# Revit family: ElectricalFixture_WiringAccessories_Hager_Sollysta_WhiteMetalcladEuroPlates
name_source: partatom
category: Electrical Fixtures
revit_build: Autodesk Revit 2015 (Build: 20160512_1515(x64)
units: mm (PartAtom-declared; Revit-internal decimal feet)

## types (9) — shared parameters
CE Approval = Yes
Colour = WhiteMetalclad
Default Elevation = 1219.2 mm  [stored 4 ft]
Design Country = China
Expected Life = 25 years
Extrusion From Wall = 9 mm  [stored 0.0295276 ft]
Finish = Polished
Frequency = 50/60Hz
Gross Weight kg = 0.165
LED Indicator Switch = No
Manufacturer = Hager
Manufacturer Country = United Kingdom
Manufacturer Website = http://www.hager.co.uk
Material = Hager_WhiteMetalClad
Overall Depth = 26.1 mm
Overall Height = 86 mm  [stored 0.282152 ft]
Packaging Recyclable = Yes
Product Family = MetalcladEuroAccomodationPlates&Modules
Product Group = WiringAccessories
Product Literature = http://www.hager.co.uk
Product Range = Sollysta
Product URL = http://www.hager.co.uk
Reference Standard = BS 1363-2
Shape = Rectangular
Shipping Weight kg = 0.188
Supply Phase = 1
Switch = Yes
Switch Width = 100 mm  [stored 0.328084 ft]
SwitchHeight = 50 mm  [stored 0.164042 ft]
Type = ElectricalFixture
Voltage (Volts) = 230V/240V

## per-type parameters (varying)
| type | 1Gang | 2Gang | 4Gang | Description | EAN Code | Features | Name | Overall Length | Overall Width | Technical Description |
| WPP1EUW | Yes | No | No | 1ModuleEuroStyleAccomodationPlateWhite | 3250617261593 | 1ModuleEuroStyleAccomodationPlateWhite | MetalcladEuroAccomodationPlates&Modules_WPP1EUW | 86 mm  [stored 0.282152 ft] | 86 mm  [stored 0.282152 ft] | 1ModuleEuroStyleAccomodationPlateWhite |
| WPP1EUBW | Yes | No | No | 1ModuleEuroStyleAccomodationPlate&BackboxWithoutKnockoutsWhite | 3250617261586 | 1ModuleEuroStyleAccomodationPlate&BackboxWithoutKnockoutsWhite | MetalcladEuroAccomodationPlates&Modules_WPP1EUBW | 86 mm  [stored 0.282152 ft] | 86 mm  [stored 0.282152 ft] | 1ModuleEuroStyleAccomodationPlate&BackboxWithoutKnockoutsWhite |
| WPP1EUBKOW | Yes | No | No | 1ModuleEuroStyleAccomodationPlate&BackboxWithKnockoutsWhite | 3250617261579 | 1ModuleEuroStyleAccomodationPlate&BackboxWithKnockoutsWhite | MetalcladEuroAccomodationPlates&Modules_WPP1EUBKOW | 86 mm  [stored 0.282152 ft] | 86 mm  [stored 0.282152 ft] | 1ModuleEuroStyleAccomodationPlate&BackboxWithKnockoutsWhite |
| WPP2EUW | No | Yes | No | 2ModuleEuroStyleAccomodationPlateWhite | 3250617261654 | 2ModuleEuroStyleAccomodationPlateWhite | MetalcladEuroAccomodationPlates&Modules_WPP2EUW | 86 mm  [stored 0.282152 ft] | 86 mm  [stored 0.282152 ft] | 2ModuleEuroStyleAccomodationPlateWhite |
| WPP2EUBW | Yes | No | No | 2ModuleEuroStyleAccomodationPlate&BackboxWithoutKnockoutsWhite | 3250617261647 | 2ModuleEuroStyleAccomodationPlate&BackboxWithoutKnockoutsWhite | MetalcladEuroAccomodationPlates&Modules_WPP2EUBW | 86 mm  [stored 0.282152 ft] | 86 mm  [stored 0.282152 ft] | 2ModuleEuroStyleAccomodationPlate&BackboxWithoutKnockoutsWhite |
| WPP2EUBKOW | No | Yes | No | 2ModuleEuroStyleAccomodationPlate&BackboxWithKnockoutsWhite | 3250617261630 | 2ModuleEuroStyleAccomodationPlate&BackboxWithKnockoutsWhite | MetalcladEuroAccomodationPlates&Modules_WPP2EUBKOW | 86 mm  [stored 0.282152 ft] | 86 mm  [stored 0.282152 ft] | 2ModuleEuroStyleAccomodationPlate&BackboxWithKnockoutsWhite |
| WPP4EUW | No | Yes | Yes | 4ModuleEuroStyleAccomodationPlateWhite | 3250617261692 | 4ModuleEuroStyleAccomodationPlateWhite | MetalcladEuroAccomodationPlates&Modules_WPP4EUW | 146 mm  [stored 0.479003 ft] | 146 mm  [stored 0.479003 ft] | 4ModuleEuroStyleAccomodationPlateWhite |
| WPP4EUBW | Yes | No | No | 4ModuleEuroStyleAccomodationPlate&BackboxWithoutKnockoutsWhite | 3250617261685 | 4ModuleEuroStyleAccomodationPlate&BackboxWithoutKnockoutsWhite | MetalcladEuroAccomodationPlates&Modules_WPP4EUBW | 86 mm  [stored 0.282152 ft] | 86 mm  [stored 0.282152 ft] | 4ModuleEuroStyleAccomodationPlate&BackboxWithoutKnockoutsWhite |
| WPP4EUBKOW | No | Yes | Yes | 4ModuleEuroStyleAccomodationPlate&BackboxWithKnockoutsWhite | 3250617261678 | 4ModuleEuroStyleAccomodationPlate&BackboxWithKnockoutsWhite | MetalcladEuroAccomodationPlates&Modules_WPP4EUBKOW | 146 mm  [stored 0.479003 ft] | 146 mm  [stored 0.479003 ft] | 4ModuleEuroStyleAccomodationPlate&BackboxWithKnockoutsWhite |

note: column(s) folded — value = type name in every type: Product Model Number, Unique Reference

note: [stored X ft] marks values corroborated as IEEE doubles in the binary element streams (Revit-internal decimal feet)

## geometry (parser evidence)
native form markers: Blend x4, Sweep x20
no freeform markers — native parametric forms only
